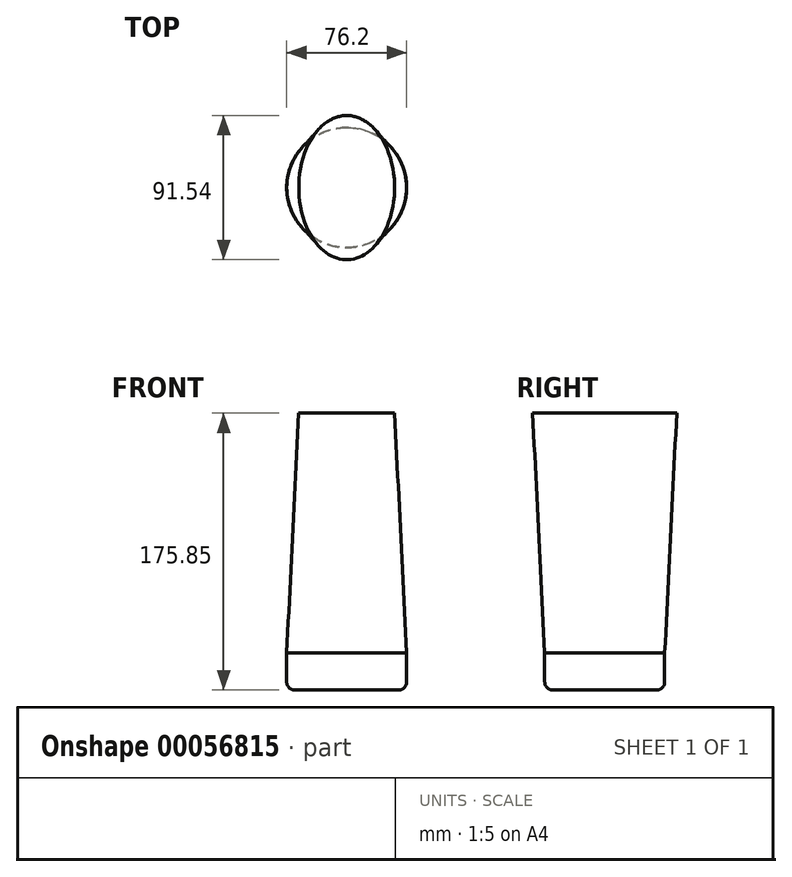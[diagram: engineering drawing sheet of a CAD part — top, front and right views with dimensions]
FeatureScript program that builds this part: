
annotation { "Feature Type Name" : "Feature", "Feature Type Description" : "" }
export const myFeature = defineFeature(function(context is Context, id is Id, definition is map)
    precondition{}
    {
        {
            var Q0;
            Q0=qCreatedBy(makeId("Top.planeOp"),FACE);
            var sketch = newSketch(context, id + "F0", { "sketchPlane" : qUnion([Q0])});
            skCircle(sketch, "E0", {"center": v(0, 0) * mm, "radius": 38.1 * mm});
            skSolve(sketch);
        }
        {
            var Q0;
            Q0 = qSketchRegion(id + "F0", true);
            extrude(context, id + "F1", {"entities" : qUnion([Q0]), "oppositeDirection" : true, "depth" : 23.45 * mm});
        }
        {
            var Q0;
            Q0=makeQuery(id+"F1.opExtrude","CAP_FACE",FACE,{"disambiguationData":[OSD([sQuery(id+"F0.wireOp",EDGE,"E0")])],"isStart":false});
            fillet(context, id + "F2", {"entities" : qUnion([Q0]), "radius" : 5.08 * mm, "tangentPropagation" : true, "allowEdgeOverflow" : false});
        }
        {
            var Q0;
            Q0=makeQuery(id+"F1.opExtrude","CAP_FACE",FACE,{"disambiguationData":[OSD([sQuery(id+"F0.wireOp",EDGE,"E0")])],"isStart":true});
            cPlane(context, id + "F3", {"entities" : qUnion([Q0]), "cplaneType" : CPlaneType.OFFSET, "offset" : 152.4 * mm, "width" : 152.4 * mm, "height" : 152.4 * mm});
        }
        {
            var Q0;
            Q0=qCreatedBy(id+"F3.planeOp",FACE);
            var sketch = newSketch(context, id + "F4", { "sketchPlane" : qUnion([Q0])});
            skEllipse(sketch, "E1", {"center": v(0, 0) * mm, "majorRadius": 45.77 * mm, "minorRadius": 30.44 * mm, "majorAxis": v(0, 1)});
            skSolve(sketch);
        }
        {
            var Q0;
            Q0=makeQuery(id+"F4.imprint","IMPRINT",FACE,{"disambiguationData":[TD([[makeQuery(id+"F4.imprint","IMPRINT",EDGE,{"derivedFrom":sQuery(id+"F4.wireOp",EDGE,"E1")}),1.0]])]});
            var Q1;
            Q1=makeQuery(id+"F1.opExtrude","CAP_FACE",FACE,{"disambiguationData":[OSD([sQuery(id+"F0.wireOp",EDGE,"E0")])],"isStart":true});
            loft(context, id + "F5", {"operationType" : NewBodyOperationType.ADD, "sheetProfilesArray" : [{ "sheetProfileEntities" : qUnion([Q0]) }, { "sheetProfileEntities" : qUnion([Q1]) }]});
        }
    });
